# Revit family: Faucet-Two_Handle-American_Standard-Chancellor-7022801_Series
name_source: partatom
category: Plumbing Fixtures
units: mm (PartAtom-declared; Revit-internal decimal feet)

## family parameters
Always vertical = No
Cut with Voids When Loaded = No
OmniClass Number = 23.45.55.17
OmniClass Title = Mixing Faucets
Part Type = Normal
Room Calculation Point = No
Round Connector Dimension = Use Diameter
Shared = Yes
Work Plane-Based = Yes

## types (2) — shared parameters
ADA Compliant = Yes
Assembly Code = D2020300
CW Connection = Yes
CWFU = 1.5
Cold Water Connection Diameter = 1/2"
Compliance Certifications = Meets ASME/CSA requirements
Default Elevation = 0"
Description = Chancellor® 8-Inch Widespread 2-Handle Bathroom Faucet 1.2 gpm/4.5 L/min With Lever Handles
Drain Depth = 3"
Drain Length = 3"
Flow Rate = 1 GPM
HW Connection = Yes
HWFU = 1.5
Height = 5 7/8"
Hot Water Connection Diameter = 1/2"
Installation Type = Deck Mount
Length = 13 1/8"
Manufacturer = American Standard
Product Documentation Link = https://lixil.cdn.celum.cloud
Product Page URL = https://www.americanstandard-us.com
URL = http://www.americanstandard-us.com
Vent Connection = No
WFU = 2
Warranty Information = Limited Lifetime Warranty
Waste Connection = No
Waste Connection Diameter = 1 1/4"
Width = 4 15/16"

## per-type parameters (varying)
| type | Finish | Material | Type Comments |
| 7022801.295 | Brass-American Standard-295-Brushed Nickel | Brass-American Standard-295-Brushed Nickel | Widespread lavatory. Metal lever handles. Speed Connect drain. Brushed Nickel finish. |
| 7022801.002 | Brass-American Standard-002-Polished Chrome | Brass-American Standard-002-Polished Chrome | Widespread lavatory. Metal lever handles. Speed Connect drain. Chrome finish. |

note: column(s) folded — value = type name in every type: Model

## geometry (parser evidence)
native form markers: Sweep x3
no freeform markers — native parametric forms only
